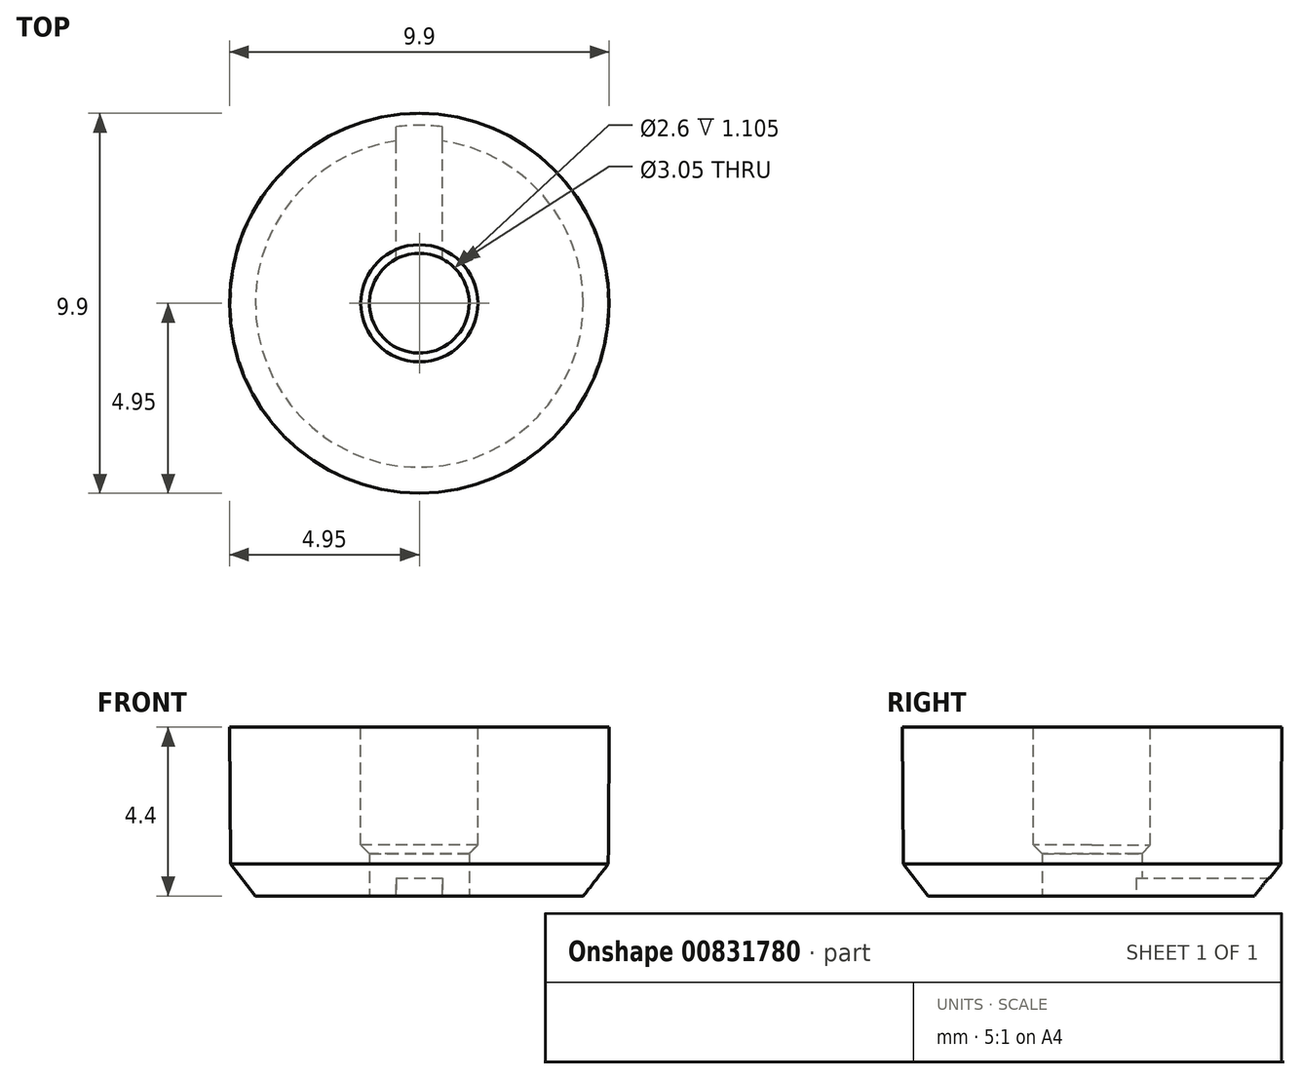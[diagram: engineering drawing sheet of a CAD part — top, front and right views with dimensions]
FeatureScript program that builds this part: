
annotation { "Feature Type Name" : "Feature", "Feature Type Description" : "" }
export const myFeature = defineFeature(function(context is Context, id is Id, definition is map)
    precondition{}
    {
        {
            var Q0;
            Q0=qCreatedBy(makeId("Top.planeOp"),FACE);
            var sketch = newSketch(context, id + "F0", { "sketchPlane" : qUnion([Q0])});
            skCircle(sketch, "E0", {"center": v(0, 0) * mm, "radius": 4.28 * mm});
            skSolve(sketch);
        }
        {
            var Q0;
            Q0=qCreatedBy(makeId("Top.planeOp"),FACE);
            cPlane(context, id + "F1", {"entities" : qUnion([Q0]), "cplaneType" : CPlaneType.OFFSET, "offset" : 0.83 * mm, "width" : 150 * mm, "height" : 150 * mm});
        }
        {
            var Q0;
            Q0=qCreatedBy(id+"F1.planeOp",FACE);
            var sketch = newSketch(context, id + "F2", { "sketchPlane" : qUnion([Q0])});
            skCircle(sketch, "E1", {"center": v(0, 0) * mm, "radius": 4.92 * mm});
            skSolve(sketch);
        }
        {
            var Q0;
            Q0=qCreatedBy(makeId("Top.planeOp"),FACE);
            cPlane(context, id + "F3", {"entities" : qUnion([Q0]), "cplaneType" : CPlaneType.OFFSET, "offset" : 4.4 * mm, "width" : 150 * mm, "height" : 150 * mm});
        }
        {
            var Q0;
            Q0=qCreatedBy(id+"F3.planeOp",FACE);
            var sketch = newSketch(context, id + "F4", { "sketchPlane" : qUnion([Q0])});
            skCircle(sketch, "E2", {"center": v(0, 0) * mm, "radius": 4.95 * mm});
            skSolve(sketch);
        }
        {
            var Q0;
            Q0=qCreatedBy(makeId("Front.planeOp"),FACE);
            var sketch = newSketch(context, id + "F5", { "sketchPlane" : qUnion([Q0])});
            skLineSegment(sketch, "E3", {"start": v(4.28, 0) * mm, "end": v(4.92, 0.83) * mm});
            skLineSegment(sketch, "E4", {"start": v(4.95, 4.4) * mm, "end": v(4.92, 0.83) * mm});
            skPoint(sketch, "E5.0.start.orphan", {"position": v(-4.95, 4.4) * mm});
            skPoint(sketch, "E6.0.start.orphan", {"position": v(-4.92, 0.83) * mm});
            skPoint(sketch, "E7.0.start.orphan", {"position": v(-4.28, 0) * mm});
            skSolve(sketch);
        }
        {
            var Q0;
            Q0 = qSketchRegion(id + "F0", true);
            var Q1;
            Q1 = qSketchRegion(id + "F2", true);
            loft(context, id + "F6", {"sheetProfilesArray" : [{ "sheetProfileEntities" : qUnion([Q0]) }, { "sheetProfileEntities" : qUnion([Q1]) }]});
        }
        {
            var Q1;
            Q1 = qSketchRegion(id + "F2", true);
            var Q2;
            Q2 = qSketchRegion(id + "F4", true);
            loft(context, id + "F7", {"operationType" : NewBodyOperationType.ADD, "sheetProfilesArray" : [{ "sheetProfileEntities" : qUnion([Q1]) }, { "sheetProfileEntities" : qUnion([Q2]) }]});
        }
        {
            var Q0;
            Q0=makeQuery(id+"F7.opLoft","CAP_FACE",FACE,{"disambiguationData":[OSD([makeQuery(id+"F4.imprint","IMPRINT",FACE,{"disambiguationData":[TD([[makeQuery(id+"F4.imprint","IMPRINT",EDGE,{"derivedFrom":sQuery(id+"F4.wireOp",EDGE,"E2")}),1.0]])]})])],"isStart":true});
            var sketch = newSketch(context, id + "F8", { "sketchPlane" : qUnion([Q0])});
            skCircle(sketch, "E8", {"center": v(0, 0) * mm, "radius": 1.53 * mm});
            skSolve(sketch);
        }
        {
            var Q0;
            Q0 = qSketchRegion(id + "F8", true);
            var Q1;
            Q1=sQuery(id+"F5.wireOp",VERTEX,"E6.0.start.orphan");
            extrude(context, id + "F9", {"entities" : qUnion([Q0]), "operationType" : NewBodyOperationType.REMOVE, "endBound" : BoundingType.UP_TO_VERTEX, "oppositeDirection" : true, "depth" : 25 * mm, "endBoundEntityVertex" : qUnion([Q1]), "offsetDistance" : 25 * mm});
        }
        {
            var Q0;
            Q0=makeQuery(id+"F6.opLoft","CAP_FACE",FACE,{"disambiguationData":[OSD([makeQuery(id+"F0.imprint","IMPRINT",FACE,{"disambiguationData":[TD([[makeQuery(id+"F0.imprint","IMPRINT",EDGE,{"derivedFrom":sQuery(id+"F0.wireOp",EDGE,"E0")}),1.0]])]})])],"isStart":true});
            var sketch = newSketch(context, id + "F10", { "sketchPlane" : qUnion([Q0])});
            skCircle(sketch, "E9", {"center": v(0, 0) * mm, "radius": 1.3 * mm});
            skSolve(sketch);
        }
        {
            var Q0;
            Q0 = qSketchRegion(id + "F10", true);
            var Q1;
            Q1=makeQuery(id+"F9.boolean.opBoolean","COPY",FACE,{"derivedFrom":makeQuery(id+"F9.opExtrude","CAP_FACE",FACE,{"disambiguationData":[OSD([sQuery(id+"F8.wireOp",EDGE,"E8")])],"isStart":false})});
            extrude(context, id + "F11", {"entities" : qUnion([Q0]), "operationType" : NewBodyOperationType.REMOVE, "endBound" : BoundingType.UP_TO_SURFACE, "oppositeDirection" : true, "depth" : 25 * mm, "endBoundEntityFace" : qUnion([Q1]), "offsetDistance" : 25 * mm});
        }
        {
            var Q0;
            Q0=makeQuery(id+"F6.opLoft","CAP_FACE",FACE,{"disambiguationData":[OSD([makeQuery(id+"F0.imprint","IMPRINT",FACE,{"disambiguationData":[TD([[makeQuery(id+"F0.imprint","IMPRINT",EDGE,{"derivedFrom":sQuery(id+"F0.wireOp",EDGE,"E0")}),1.0]])]})])],"isStart":true});
            var sketch = newSketch(context, id + "F12", { "sketchPlane" : qUnion([Q0])});
            skLineSegment(sketch, "E10", {"start": v(0, -5) * mm, "end": v(0.6, -5) * mm});
            skLineSegment(sketch, "E11", {"start": v(0, 0) * mm, "end": v(-0.6, 0) * mm});
            skLineSegment(sketch, "E12.bottom", {"start": v(-0.6, 0) * mm, "end": v(0.6, 0) * mm});
            skLineSegment(sketch, "E12.top", {"start": v(-0.6, -5) * mm, "end": v(0.6, -5) * mm});
            skLineSegment(sketch, "E12.left", {"start": v(-0.6, 0) * mm, "end": v(-0.6, -5) * mm});
            skLineSegment(sketch, "E12.right", {"start": v(0.6, 0) * mm, "end": v(0.6, -5) * mm});
            skSolve(sketch);
        }
        {
            var Q0;
            Q0 = qSketchRegion(id + "F12", true);
            extrude(context, id + "F13", {"entities" : qUnion([Q0]), "operationType" : NewBodyOperationType.REMOVE, "oppositeDirection" : true, "depth" : 0.46 * mm, "offsetDistance" : 25 * mm});
        }
        {
            var Q0;
            Q0=makeQuery(id+"F9.boolean.opBoolean","COPY",EDGE,{"derivedFrom":makeQuery(id+"F9.opExtrude","CAP_EDGE",EDGE,{"disambiguationData":[OSD([sQuery(id+"F8.wireOp",EDGE,"E8")])],"isStart":false})});
            chamfer(context, id + "F14", {"entities" : qUnion([Q0]), "width" : 0.5 * mm, "tangentPropagation" : true});
        }
    });
